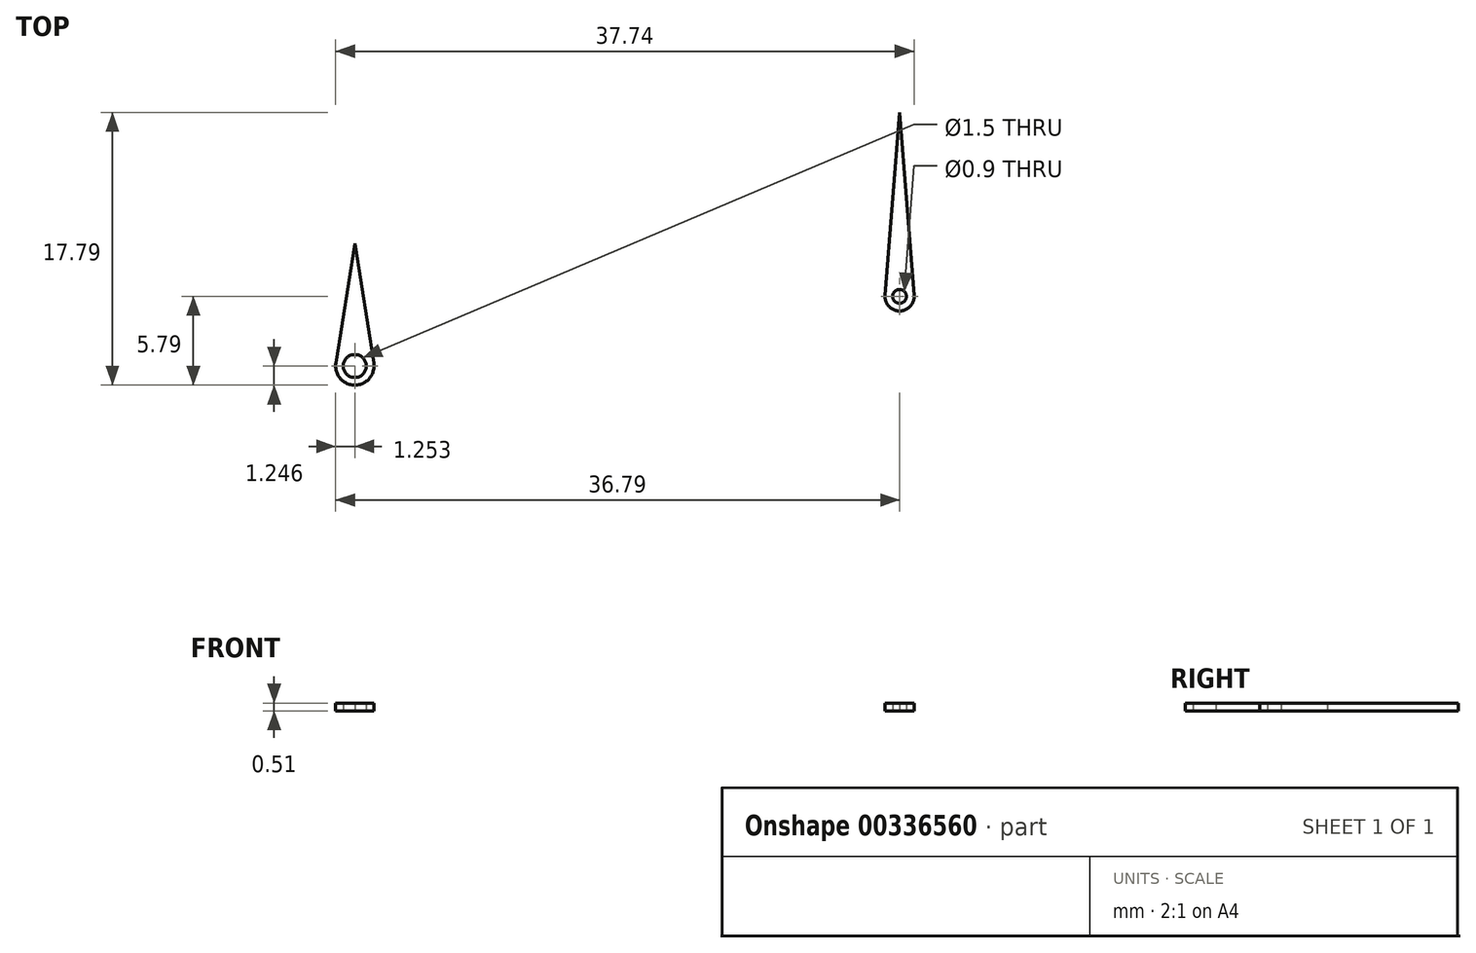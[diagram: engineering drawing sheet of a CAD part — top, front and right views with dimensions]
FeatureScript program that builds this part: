
annotation { "Feature Type Name" : "Feature", "Feature Type Description" : "" }
export const myFeature = defineFeature(function(context is Context, id is Id, definition is map)
    precondition{}
    {
        {
            var Q0;
            Q0=qCreatedBy(makeId("Top.planeOp"),FACE);
            var sketch = newSketch(context, id + "F0", { "sketchPlane" : qUnion([Q0])});
            skCircle(sketch, "E0", {"center": v(0, 0) * mm, "radius": 0.45 * mm});
            skArc(sketch, "E1", {"start": v(-0.95, 0.08) * mm, "mid": v(0, -0.95) * mm, "end": v(0.95, 0.08) * mm});
            skLineSegment(sketch, "E2", {"start": v(0, 0) * mm, "end": v(0, 12) * mm, "construction": true});
            skLineSegment(sketch, "E3", {"start": v(0, 12) * mm, "end": v(-0.95, 0.08) * mm});
            skLineSegment(sketch, "E4.MirrorCS", {"start": v(0, 12) * mm, "end": v(0.95, 0.08) * mm});
            skSolve(sketch);
        }
        {
            var Q0;
            Q0 = qSketchRegion(id + "F0", true);
            extrude(context, id + "F1", {"entities" : qUnion([Q0]), "depth" : .51 * mm});
        }
        {
            var Q0;
            Q0=qCreatedBy(makeId("Top.planeOp"),FACE);
            var sketch = newSketch(context, id + "F2", { "sketchPlane" : qUnion([Q0])});
            skCircle(sketch, "E5", {"center": v(-35.54, -4.54) * mm, "radius": 0.75 * mm});
            skArc(sketch, "E6", {"start": v(-36.77, -4.35) * mm, "mid": v(-35.54, -5.8) * mm, "end": v(-34.3, -4.35) * mm});
            skLineSegment(sketch, "E7", {"start": v(-35.54, -4.54) * mm, "end": v(-35.54, 3.46) * mm, "construction": true});
            skLineSegment(sketch, "E8", {"start": v(-35.54, 3.46) * mm, "end": v(-36.77, -4.35) * mm});
            skLineSegment(sketch, "E9.MirrorCS", {"start": v(-35.54, 3.46) * mm, "end": v(-34.3, -4.35) * mm});
            skSolve(sketch);
        }
        {
            var Q0;
            Q0 = qSketchRegion(id + "F2", true);
            extrude(context, id + "F3", {"entities" : qUnion([Q0]), "depth" : 0.51 * mm});
        }
    });
